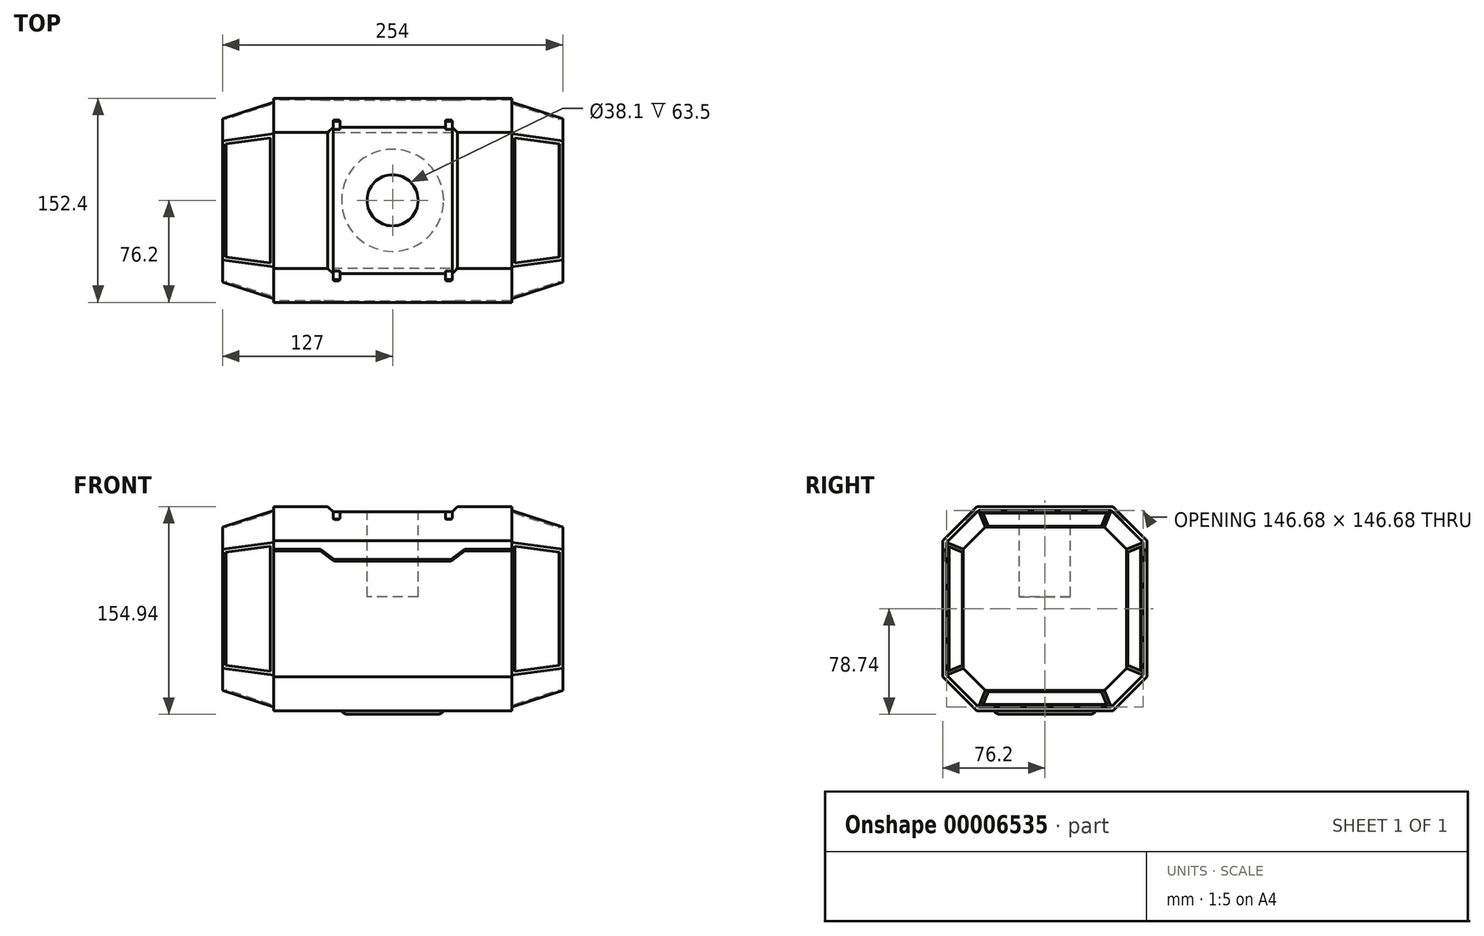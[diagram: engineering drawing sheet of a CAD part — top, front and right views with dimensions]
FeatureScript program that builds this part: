
annotation { "Feature Type Name" : "Feature", "Feature Type Description" : "" }
export const myFeature = defineFeature(function(context is Context, id is Id, definition is map)
    precondition{}
    {
        {
            var Q0;
            Q0=qCreatedBy(makeId("Top.planeOp"),FACE);
            var sketch = newSketch(context, id + "F0", { "sketchPlane" : qUnion([Q0])});
            skLineSegment(sketch, "E0.bottom", {"start": v(-88.9, -76.2) * mm, "end": v(88.9, -76.2) * mm});
            skLineSegment(sketch, "E0.top", {"start": v(-88.9, 76.2) * mm, "end": v(88.9, 76.2) * mm});
            skLineSegment(sketch, "E0.left", {"start": v(-88.9, -76.2) * mm, "end": v(-88.9, 76.2) * mm});
            skLineSegment(sketch, "E0.right", {"start": v(88.9, -76.2) * mm, "end": v(88.9, 76.2) * mm});
            skSolve(sketch);
        }
        {
            var Q0;
            Q0=makeQuery(id+"F0.imprint","IMPRINT",FACE,{"disambiguationData":[TD([[makeQuery(id+"F0.imprint","IMPRINT",EDGE,{"derivedFrom":sQuery(id+"F0.wireOp",EDGE,"E0.bottom")}),1.0]])]});
            extrude(context, id + "F1", {"entities" : qUnion([Q0]), "depth" : 152.4 * mm});
        }
        {
            var Q0;
            Q0=makeQuery(id+"F1.opExtrude","CAP_EDGE",EDGE,{"disambiguationData":[OSD([sQuery(id+"F0.wireOp",EDGE,"E0.bottom")])],"isStart":false});
            var Q1;
            Q1=makeQuery(id+"F1.opExtrude","CAP_EDGE",EDGE,{"disambiguationData":[OSD([sQuery(id+"F0.wireOp",EDGE,"E0.top")])],"isStart":false});
            var Q2;
            Q2=makeQuery(id+"F1.opExtrude","CAP_EDGE",EDGE,{"disambiguationData":[OSD([sQuery(id+"F0.wireOp",EDGE,"E0.bottom")])],"isStart":true});
            var Q3;
            Q3=makeQuery(id+"F1.opExtrude","CAP_EDGE",EDGE,{"disambiguationData":[OSD([sQuery(id+"F0.wireOp",EDGE,"E0.top")])],"isStart":true});
            chamfer(context, id + "F2", {"entities" : qUnion([Q0, Q1, Q2, Q3]), "width" : 25.4 * mm, "tangentPropagation" : true});
        }
        {
            var Q0;
            Q0=makeQuery(id+"F1.opExtrude","SWEPT_FACE",FACE,{"disambiguationData":[OSD([sQuery(id+"F0.wireOp",EDGE,"E0.left")])]});
            var sketch = newSketch(context, id + "F3", { "sketchPlane" : qUnion([Q0])});
            skLineSegment(sketch, "E1.0", {"start": v(-49.75, 149.86) * mm, "end": v(-73.66, 125.95) * mm});
            skLineSegment(sketch, "E1.1", {"start": v(49.75, 149.86) * mm, "end": v(-49.75, 149.86) * mm});
            skLineSegment(sketch, "E1.2", {"start": v(73.66, 125.95) * mm, "end": v(49.75, 149.86) * mm});
            skLineSegment(sketch, "E1.3", {"start": v(73.66, 26.45) * mm, "end": v(73.66, 125.95) * mm});
            skLineSegment(sketch, "E1.4", {"start": v(49.75, 2.54) * mm, "end": v(73.66, 26.45) * mm});
            skLineSegment(sketch, "E1.5", {"start": v(-73.66, 125.95) * mm, "end": v(-73.66, 26.45) * mm});
            skLineSegment(sketch, "E1.6", {"start": v(-49.75, 2.54) * mm, "end": v(49.75, 2.54) * mm});
            skLineSegment(sketch, "E1.7", {"start": v(-73.66, 26.45) * mm, "end": v(-49.75, 2.54) * mm});
            skSolve(sketch);
        }
        {
            var Q0;
            Q0=makeQuery(id+"F3.imprint","IMPRINT",FACE,{"disambiguationData":[TD([[makeQuery(id+"F3.imprint","IMPRINT",EDGE,{"derivedFrom":sQuery(id+"F3.wireOp",EDGE,"E1.0")}),1.0]])]});
            extrude(context, id + "F4", {"entities" : qUnion([Q0]), "operationType" : NewBodyOperationType.ADD, "depth" : 38.1 * mm});
        }
        {
            var Q0;
            Q0=makeQuery(id+"F4.opExtrude","CAP_FACE",FACE,{"disambiguationData":[OSD([sQuery(id+"F3.wireOp",EDGE,"E1.0"),sQuery(id+"F3.wireOp",EDGE,"E1.1"),sQuery(id+"F3.wireOp",EDGE,"E1.2"),sQuery(id+"F3.wireOp",EDGE,"E1.3"),sQuery(id+"F3.wireOp",EDGE,"E1.4"),sQuery(id+"F3.wireOp",EDGE,"E1.5"),sQuery(id+"F3.wireOp",EDGE,"E1.6"),sQuery(id+"F3.wireOp",EDGE,"E1.7")])],"isStart":false});
            chamfer(context, id + "F5", {"entities" : qUnion([Q0]), "chamferType" : ChamferType.OFFSET_ANGLE, "width" : 12.7 * mm, "oppositeDirection" : false, "angle" : 72 * degree, "tangentPropagation" : true});
        }
        {
            var Q0;
            Q0=makeQuery(id+"F1.opExtrude","SWEPT_FACE",FACE,{"disambiguationData":[OSD([sQuery(id+"F0.wireOp",EDGE,"E0.right")])]});
            var sketch = newSketch(context, id + "F6", { "sketchPlane" : qUnion([Q0])});
            skLineSegment(sketch, "E2.0", {"start": v(-73.66, 26.45) * mm, "end": v(-49.75, 2.54) * mm});
            skLineSegment(sketch, "E2.1", {"start": v(-73.66, 125.95) * mm, "end": v(-73.66, 26.45) * mm});
            skLineSegment(sketch, "E2.2", {"start": v(-49.75, 149.86) * mm, "end": v(-73.66, 125.95) * mm});
            skLineSegment(sketch, "E2.3", {"start": v(49.75, 149.86) * mm, "end": v(-49.75, 149.86) * mm});
            skLineSegment(sketch, "E2.4", {"start": v(73.66, 125.95) * mm, "end": v(49.75, 149.86) * mm});
            skLineSegment(sketch, "E2.5", {"start": v(-49.75, 2.54) * mm, "end": v(49.75, 2.54) * mm});
            skLineSegment(sketch, "E2.6", {"start": v(73.66, 26.45) * mm, "end": v(73.66, 125.95) * mm});
            skLineSegment(sketch, "E2.7", {"start": v(49.75, 2.54) * mm, "end": v(73.66, 26.45) * mm});
            skSolve(sketch);
        }
        {
            var Q0;
            Q0=makeQuery(id+"F6.imprint","IMPRINT",FACE,{"disambiguationData":[TD([[makeQuery(id+"F6.imprint","IMPRINT",EDGE,{"derivedFrom":sQuery(id+"F6.wireOp",EDGE,"E2.0")}),1.0]])]});
            extrude(context, id + "F7", {"entities" : qUnion([Q0]), "operationType" : NewBodyOperationType.ADD, "depth" : 38.1 * mm});
        }
        {
            var Q0;
            Q0=makeQuery(id+"F7.opExtrude","CAP_FACE",FACE,{"disambiguationData":[OSD([sQuery(id+"F6.wireOp",EDGE,"E2.0"),sQuery(id+"F6.wireOp",EDGE,"E2.1"),sQuery(id+"F6.wireOp",EDGE,"E2.2"),sQuery(id+"F6.wireOp",EDGE,"E2.3"),sQuery(id+"F6.wireOp",EDGE,"E2.4"),sQuery(id+"F6.wireOp",EDGE,"E2.5"),sQuery(id+"F6.wireOp",EDGE,"E2.6"),sQuery(id+"F6.wireOp",EDGE,"E2.7")])],"isStart":false});
            chamfer(context, id + "F8", {"entities" : qUnion([Q0]), "chamferType" : ChamferType.OFFSET_ANGLE, "width" : 12.7 * mm, "oppositeDirection" : false, "angle" : 72 * degree, "tangentPropagation" : true});
        }
        {
            var Q0;
            Q0=makeQuery(id+"F1.opExtrude","CAP_FACE",FACE,{"disambiguationData":[OSD([sQuery(id+"F0.wireOp",EDGE,"E0.bottom"),sQuery(id+"F0.wireOp",EDGE,"E0.top"),sQuery(id+"F0.wireOp",EDGE,"E0.left"),sQuery(id+"F0.wireOp",EDGE,"E0.right")])],"isStart":true});
            var sketch = newSketch(context, id + "F9", { "sketchPlane" : qUnion([Q0])});
            skCircle(sketch, "E3", {"center": v(0, 0) * mm, "radius": 38.1 * mm});
            skSolve(sketch);
        }
        {
            var Q0;
            Q0=makeQuery(id+"F9.imprint","IMPRINT",FACE,{"disambiguationData":[TD([[makeQuery(id+"F9.imprint","IMPRINT",EDGE,{"derivedFrom":sQuery(id+"F9.wireOp",EDGE,"E3")}),1.0]])]});
            extrude(context, id + "F10", {"entities" : qUnion([Q0]), "operationType" : NewBodyOperationType.ADD, "depth" : 2.54 * mm});
        }
        {
            var Q0;
            Q0=makeQuery(id+"F10.opExtrude","CAP_EDGE",EDGE,{"disambiguationData":[OSD([sQuery(id+"F9.wireOp",EDGE,"E3")])],"isStart":false});
            fillet(context, id + "F11", {"entities" : qUnion([Q0]), "radius" : 5.08 * mm, "tangentPropagation" : true, "allowEdgeOverflow" : false});
        }
        {
            var Q0;
            Q0=makeQuery(id+"F1.opExtrude","SWEPT_FACE",FACE,{"disambiguationData":[OSD([sQuery(id+"F0.wireOp",EDGE,"E0.bottom")])]});
            var sketch = newSketch(context, id + "F12", { "sketchPlane" : qUnion([Q0])});
            skLineSegment(sketch, "E4", {"start": v(0, 148.6) * mm, "end": v(44.45, 148.6) * mm});
            skLineSegment(sketch, "E5", {"start": v(44.45, 148.6) * mm, "end": v(51.87, 155.65) * mm});
            skLineSegment(sketch, "E6.0.MirrorCS", {"start": v(0, 148.6) * mm, "end": v(-44.45, 148.6) * mm});
            skLineSegment(sketch, "E7.0.MirrorCS", {"start": v(-44.45, 148.6) * mm, "end": v(-51.87, 155.65) * mm});
            skLineSegment(sketch, "E8", {"start": v(-51.87, 155.65) * mm, "end": v(51.87, 155.65) * mm});
            skSolve(sketch);
        }
        {
            var Q0;
            Q0=makeQuery(id+"F12.imprint","IMPRINT",FACE,{"disambiguationData":[TD([[makeQuery(id+"F12.imprint","IMPRINT",EDGE,{"derivedFrom":sQuery(id+"F12.wireOp",EDGE,"E4")}),1.0]])]});
            extrude(context, id + "F13", {"entities" : qUnion([Q0]), "operationType" : NewBodyOperationType.REMOVE, "oppositeDirection" : true, "depth" : 152.4 * mm});
        }
        {
            var Q0;
            {var subQ0=sQuery(id+"F0.wireOp",EDGE,"E0.top");Q0=makeQuery(id+"F2.opChamfer","BLEND_FACE",FACE,{"disambiguationData":[OSD([subQ0]),TDD([makeQuery(id+"F1.opExtrude","CAP_EDGE",EDGE,{"disambiguationData":[OSD([subQ0])],"isStart":false})])]});}
            var sketch = newSketch(context, id + "F14", { "sketchPlane" : qUnion([Q0])});
            skLineSegment(sketch, "E9.bottom", {"start": v(-44.45, 66.45) * mm, "end": v(-39.37, 66.45) * mm});
            skLineSegment(sketch, "E9.top", {"start": v(-43.18, 58.83) * mm, "end": v(-40.64, 58.83) * mm});
            skLineSegment(sketch, "E9.left", {"start": v(-44.45, 66.45) * mm, "end": v(-44.45, 60.1) * mm});
            skLineSegment(sketch, "E9.right", {"start": v(-39.37, 66.45) * mm, "end": v(-39.37, 60.1) * mm});
            skLineSegment(sketch, "E10.bottom", {"start": v(44.45, 66.45) * mm, "end": v(39.37, 66.45) * mm});
            skLineSegment(sketch, "E10.top", {"start": v(43.18, 58.83) * mm, "end": v(40.64, 58.83) * mm});
            skLineSegment(sketch, "E10.left", {"start": v(44.45, 66.45) * mm, "end": v(44.45, 60.1) * mm});
            skLineSegment(sketch, "E10.right", {"start": v(39.37, 66.45) * mm, "end": v(39.37, 60.1) * mm});
            skPoint(sketch, "E11.visualSharp", {"position": v(-44.45, 58.83) * mm});
            skArc(sketch, "E11.filletArc", {"start": v(-44.45, 60.1) * mm, "mid": v(-44.08, 59.2) * mm, "end": v(-43.18, 58.83) * mm});
            skPoint(sketch, "E12.visualSharp", {"position": v(-39.37, 58.83) * mm});
            skArc(sketch, "E12.filletArc", {"start": v(-40.64, 58.83) * mm, "mid": v(-39.74, 59.2) * mm, "end": v(-39.37, 60.1) * mm});
            skPoint(sketch, "E13.visualSharp", {"position": v(39.37, 58.83) * mm});
            skArc(sketch, "E13.filletArc", {"start": v(39.37, 60.1) * mm, "mid": v(39.74, 59.2) * mm, "end": v(40.64, 58.83) * mm});
            skPoint(sketch, "E14.visualSharp", {"position": v(44.45, 58.83) * mm});
            skArc(sketch, "E14.filletArc", {"start": v(43.18, 58.83) * mm, "mid": v(44.08, 59.2) * mm, "end": v(44.45, 60.1) * mm});
            skLineSegment(sketch, "E15.top", {"start": v(-44.45, 69.9) * mm, "end": v(-39.37, 69.9) * mm});
            skLineSegment(sketch, "E15.left", {"start": v(-44.45, 66.45) * mm, "end": v(-44.45, 69.9) * mm});
            skLineSegment(sketch, "E15.right", {"start": v(-39.37, 66.45) * mm, "end": v(-39.37, 69.9) * mm});
            skLineSegment(sketch, "E16.top", {"start": v(44.45, 69.9) * mm, "end": v(39.37, 69.9) * mm});
            skLineSegment(sketch, "E16.left", {"start": v(44.45, 66.45) * mm, "end": v(44.45, 69.9) * mm});
            skLineSegment(sketch, "E16.right", {"start": v(39.37, 66.45) * mm, "end": v(39.37, 69.9) * mm});
            skSolve(sketch);
        }
        {
            var Q0;
            Q0=makeQuery(id+"F14.imprint","IMPRINT",FACE,{"disambiguationData":[TD([[makeQuery(id+"F14.imprint","IMPRINT",EDGE,{"derivedFrom":sQuery(id+"F14.wireOp",EDGE,"E9.top")}),1.0]])]});
            var Q1;
            Q1=makeQuery(id+"F14.imprint","IMPRINT",FACE,{"disambiguationData":[TD([[makeQuery(id+"F14.imprint","IMPRINT",EDGE,{"derivedFrom":sQuery(id+"F14.wireOp",EDGE,"E9.bottom")}),-1.0]])]});
            var Q2;
            Q2=makeQuery(id+"F14.imprint","IMPRINT",FACE,{"disambiguationData":[TD([[makeQuery(id+"F14.imprint","IMPRINT",EDGE,{"derivedFrom":sQuery(id+"F14.wireOp",EDGE,"E10.top")}),-1.0]])]});
            var Q3;
            Q3=makeQuery(id+"F14.imprint","IMPRINT",FACE,{"disambiguationData":[TD([[makeQuery(id+"F14.imprint","IMPRINT",EDGE,{"derivedFrom":sQuery(id+"F14.wireOp",EDGE,"E10.bottom")}),-1.0]])]});
            extrude(context, id + "F15", {"entities" : qUnion([Q0, Q1, Q2, Q3]), "operationType" : NewBodyOperationType.REMOVE, "oppositeDirection" : true, "depth" : 1.27 * mm});
        }
        {
            var Q0;
            {var subQ0=sQuery(id+"F0.wireOp",EDGE,"E0.bottom");Q0=makeQuery(id+"F2.opChamfer","BLEND_FACE",FACE,{"disambiguationData":[OSD([subQ0]),TDD([makeQuery(id+"F1.opExtrude","CAP_EDGE",EDGE,{"disambiguationData":[OSD([subQ0])],"isStart":false})])]});}
            var sketch = newSketch(context, id + "F16", { "sketchPlane" : qUnion([Q0])});
            skLineSegment(sketch, "E17.bottom", {"start": v(-44.45, 66.45) * mm, "end": v(-39.37, 66.45) * mm});
            skLineSegment(sketch, "E17.top", {"start": v(-43.18, 58.83) * mm, "end": v(-40.64, 58.83) * mm});
            skLineSegment(sketch, "E17.left", {"start": v(-44.45, 66.45) * mm, "end": v(-44.45, 60.1) * mm});
            skLineSegment(sketch, "E17.right", {"start": v(-39.37, 66.45) * mm, "end": v(-39.37, 60.1) * mm});
            skLineSegment(sketch, "E18.bottom", {"start": v(44.45, 66.45) * mm, "end": v(39.37, 66.45) * mm});
            skLineSegment(sketch, "E18.top", {"start": v(43.18, 58.83) * mm, "end": v(40.64, 58.83) * mm});
            skLineSegment(sketch, "E18.left", {"start": v(44.45, 66.45) * mm, "end": v(44.45, 60.1) * mm});
            skLineSegment(sketch, "E18.right", {"start": v(39.37, 66.45) * mm, "end": v(39.37, 60.1) * mm});
            skPoint(sketch, "E19.visualSharp", {"position": v(-44.45, 58.83) * mm});
            skArc(sketch, "E19.filletArc", {"start": v(-44.45, 60.1) * mm, "mid": v(-44.08, 59.2) * mm, "end": v(-43.18, 58.83) * mm});
            skPoint(sketch, "E20.visualSharp", {"position": v(-39.37, 58.83) * mm});
            skArc(sketch, "E20.filletArc", {"start": v(-40.64, 58.83) * mm, "mid": v(-39.74, 59.2) * mm, "end": v(-39.37, 60.1) * mm});
            skPoint(sketch, "E21.visualSharp", {"position": v(39.37, 58.83) * mm});
            skArc(sketch, "E21.filletArc", {"start": v(39.37, 60.1) * mm, "mid": v(39.74, 59.2) * mm, "end": v(40.64, 58.83) * mm});
            skPoint(sketch, "E22.visualSharp", {"position": v(44.45, 58.83) * mm});
            skArc(sketch, "E22.filletArc", {"start": v(43.18, 58.83) * mm, "mid": v(44.08, 59.2) * mm, "end": v(44.45, 60.1) * mm});
            skLineSegment(sketch, "E23.top", {"start": v(-44.45, 70.2) * mm, "end": v(-39.37, 70.2) * mm});
            skLineSegment(sketch, "E23.left", {"start": v(-44.45, 66.45) * mm, "end": v(-44.45, 70.2) * mm});
            skLineSegment(sketch, "E23.right", {"start": v(-39.37, 66.45) * mm, "end": v(-39.37, 70.2) * mm});
            skLineSegment(sketch, "E24.top", {"start": v(44.45, 71) * mm, "end": v(39.37, 71) * mm});
            skLineSegment(sketch, "E24.left", {"start": v(44.45, 66.45) * mm, "end": v(44.45, 71) * mm});
            skLineSegment(sketch, "E24.right", {"start": v(39.37, 66.45) * mm, "end": v(39.37, 71) * mm});
            skSolve(sketch);
        }
        {
            var Q0;
            Q0=makeQuery(id+"F16.imprint","IMPRINT",FACE,{"disambiguationData":[TD([[makeQuery(id+"F16.imprint","IMPRINT",EDGE,{"derivedFrom":sQuery(id+"F16.wireOp",EDGE,"E17.top")}),1.0]])]});
            var Q1;
            Q1=makeQuery(id+"F16.imprint","IMPRINT",FACE,{"disambiguationData":[TD([[makeQuery(id+"F16.imprint","IMPRINT",EDGE,{"derivedFrom":sQuery(id+"F16.wireOp",EDGE,"E17.bottom")}),-1.0]])]});
            var Q2;
            Q2=makeQuery(id+"F16.imprint","IMPRINT",FACE,{"disambiguationData":[TD([[makeQuery(id+"F16.imprint","IMPRINT",EDGE,{"derivedFrom":sQuery(id+"F16.wireOp",EDGE,"E18.top")}),-1.0]])]});
            var Q3;
            Q3=makeQuery(id+"F16.imprint","IMPRINT",FACE,{"disambiguationData":[TD([[makeQuery(id+"F16.imprint","IMPRINT",EDGE,{"derivedFrom":sQuery(id+"F16.wireOp",EDGE,"E18.bottom")}),-1.0]])]});
            extrude(context, id + "F17", {"entities" : qUnion([Q0, Q1, Q2, Q3]), "operationType" : NewBodyOperationType.REMOVE, "oppositeDirection" : true, "depth" : 1.27 * mm});
        }
        {
            var Q0;
            Q0=makeQuery(id+"F1.opExtrude","SWEPT_FACE",FACE,{"disambiguationData":[OSD([sQuery(id+"F0.wireOp",EDGE,"E0.bottom")])]});
            var sketch = newSketch(context, id + "F18", { "sketchPlane" : qUnion([Q0])});
            skLineSegment(sketch, "E25", {"start": v(88.9, 120.65) * mm, "end": v(53.9, 120.65) * mm});
            skLineSegment(sketch, "E26", {"start": v(0, 113.03) * mm, "end": v(43.78, 113.03) * mm});
            skLineSegment(sketch, "E27", {"start": v(43.78, 113.03) * mm, "end": v(53.9, 120.65) * mm});
            skLineSegment(sketch, "E28.0.MirrorCS", {"start": v(0, 113.03) * mm, "end": v(-43.78, 113.03) * mm});
            skLineSegment(sketch, "E29.0.MirrorCS", {"start": v(-43.78, 113.03) * mm, "end": v(-53.9, 120.65) * mm});
            skLineSegment(sketch, "E30.trimOffspring", {"start": v(-53.9, 120.65) * mm, "end": v(-88.9, 120.65) * mm});
            skPoint(sketch, "E31.orphan", {"position": v(0, 120.65) * mm});
            skLineSegment(sketch, "E32.0", {"start": v(0, 111.76) * mm, "end": v(43.78, 111.76) * mm});
            skLineSegment(sketch, "E32.1", {"start": v(0, 111.76) * mm, "end": v(-43.78, 111.76) * mm});
            skLineSegment(sketch, "E33.0", {"start": v(88.9, 119.38) * mm, "end": v(53.94, 119.38) * mm});
            skLineSegment(sketch, "E34.0", {"start": v(-53.9, 119.38) * mm, "end": v(-88.9, 119.38) * mm});
            skLineSegment(sketch, "E35", {"start": v(-53.9, 119.38) * mm, "end": v(-43.78, 111.76) * mm});
            skLineSegment(sketch, "E36", {"start": v(53.94, 119.38) * mm, "end": v(43.78, 111.76) * mm});
            skSolve(sketch);
        }
        {
            var Q0;
            Q0=makeQuery(id+"F1.opExtrude","SWEPT_FACE",FACE,{"disambiguationData":[OSD([sQuery(id+"F0.wireOp",EDGE,"E0.top")])]});
            var sketch = newSketch(context, id + "F19", { "sketchPlane" : qUnion([Q0])});
            skLineSegment(sketch, "E37.0", {"start": v(0, 111.76) * mm, "end": v(43.78, 111.76) * mm});
            skLineSegment(sketch, "E38.0", {"start": v(0, 113.03) * mm, "end": v(-43.78, 113.03) * mm});
            skLineSegment(sketch, "E39.0", {"start": v(0, 111.76) * mm, "end": v(-43.78, 111.76) * mm});
            skLineSegment(sketch, "E40.0", {"start": v(-53.94, 119.38) * mm, "end": v(-43.78, 111.76) * mm});
            skLineSegment(sketch, "E40.1", {"start": v(-43.78, 113.03) * mm, "end": v(-53.9, 120.65) * mm});
            skLineSegment(sketch, "E41.0", {"start": v(-88.9, 119.38) * mm, "end": v(-53.94, 119.38) * mm});
            skLineSegment(sketch, "E41.1", {"start": v(-88.9, 120.65) * mm, "end": v(-53.9, 120.65) * mm});
            skLineSegment(sketch, "E42.0", {"start": v(53.9, 119.38) * mm, "end": v(88.9, 119.38) * mm});
            skLineSegment(sketch, "E42.1", {"start": v(53.9, 120.65) * mm, "end": v(88.9, 120.65) * mm});
            skLineSegment(sketch, "E43.0", {"start": v(53.9, 119.38) * mm, "end": v(43.78, 111.76) * mm});
            skLineSegment(sketch, "E43.1", {"start": v(43.78, 113.03) * mm, "end": v(53.9, 120.65) * mm});
            skLineSegment(sketch, "E43.2", {"start": v(0, 113.03) * mm, "end": v(43.78, 113.03) * mm});
            skSolve(sketch);
        }
        {
            var Q0;
            Q0=makeQuery(id+"F19.imprint","IMPRINT",FACE,{"disambiguationData":[TD([[makeQuery(id+"F19.imprint","IMPRINT",EDGE,{"derivedFrom":sQuery(id+"F19.wireOp",EDGE,"E37.0")}),1.0]])]});
            extrude(context, id + "F20", {"entities" : qUnion([Q0]), "operationType" : NewBodyOperationType.REMOVE, "oppositeDirection" : true, "depth" : 1.27 * mm});
        }
        {
            var Q0;
            {var subQ6=sQuery(id+"F18.wireOp",EDGE,"E25");Q0=makeQuery(id+"F18.imprint","IMPRINT",FACE,{"disambiguationData":[TD([[makeQuery(id+"F18.imprint","IMPRINT",EDGE,{"derivedFrom":subQ6}),1.0]])]});}
            extrude(context, id + "F21", {"entities" : qUnion([Q0]), "operationType" : NewBodyOperationType.REMOVE, "oppositeDirection" : true, "depth" : 1.27 * mm});
        }
        {
            var Q0;
            Q0=makeQuery(id+"F13.boolean.opBoolean","COPY",FACE,{"derivedFrom":makeQuery(id+"F13.opExtrude","SWEPT_FACE",FACE,{"disambiguationData":[OSD([sQuery(id+"F12.wireOp",EDGE,"E4"),sQuery(id+"F12.wireOp",EDGE,"E6.0.MirrorCS")])]})});
            var sketch = newSketch(context, id + "F22", { "sketchPlane" : qUnion([Q0])});
            skCircle(sketch, "E44", {"center": v(0, 0) * mm, "radius": 19.05 * mm});
            skSolve(sketch);
        }
        {
            var Q0;
            Q0=makeQuery(id+"F22.imprint","IMPRINT",FACE,{"disambiguationData":[TD([[makeQuery(id+"F22.imprint","IMPRINT",EDGE,{"derivedFrom":sQuery(id+"F22.wireOp",EDGE,"E44")}),1.0]])]});
            extrude(context, id + "F23", {"entities" : qUnion([Q0]), "operationType" : NewBodyOperationType.REMOVE, "oppositeDirection" : true, "depth" : 63.5 * mm});
        }
        {
            var Q0;
            Q0=makeQuery(id+"F8.opChamfer","BLEND_FACE",FACE,{"disambiguationData":[OSD([sQuery(id+"F6.wireOp",EDGE,"E2.3")])]});
            var sketch = newSketch(context, id + "F24", { "sketchPlane" : qUnion([Q0])});
            skLineSegment(sketch, "E45.0", {"start": v(40.88, -46.73) * mm, "end": v(75.86, -42.25) * mm});
            skLineSegment(sketch, "E45.1", {"start": v(40.88, 46.73) * mm, "end": v(40.88, -46.73) * mm});
            skLineSegment(sketch, "E45.2", {"start": v(40.88, 46.73) * mm, "end": v(75.86, 42.25) * mm});
            skLineSegment(sketch, "E45.3", {"start": v(75.86, -42.25) * mm, "end": v(75.86, 42.25) * mm});
            skSolve(sketch);
        }
        {
            var Q0;
            Q0=makeQuery(id+"F24.imprint","IMPRINT",FACE,{"disambiguationData":[TD([[makeQuery(id+"F24.imprint","IMPRINT",EDGE,{"derivedFrom":sQuery(id+"F24.wireOp",EDGE,"E45.0")}),1.0]])]});
            extrude(context, id + "F25", {"entities" : qUnion([Q0]), "operationType" : NewBodyOperationType.REMOVE, "oppositeDirection" : true, "depth" : 1.27 * mm});
        }
        {
            var Q0;
            Q0=qCreatedBy(makeId("Front.planeOp"),FACE);
            var sketch = newSketch(context, id + "F26", { "sketchPlane" : qUnion([Q0])});
            skLineSegment(sketch, "E46", {"start": v(0, 76.2) * mm, "end": v(-188.8, 76.2) * mm});
            skSolve(sketch);
        }
        {
            var Q0;
            Q0=makeQuery(id+"F25.boolean.opBoolean","COPY",FACE,{"derivedFrom":makeQuery(id+"F25.opExtrude","CAP_FACE",FACE,{"disambiguationData":[OSD([sQuery(id+"F24.wireOp",EDGE,"E45.0"),sQuery(id+"F24.wireOp",EDGE,"E45.1"),sQuery(id+"F24.wireOp",EDGE,"E45.2"),sQuery(id+"F24.wireOp",EDGE,"E45.3")])],"isStart":false})});
            var Q1;
            Q1=makeQuery(id+"F25.boolean.opBoolean","COPY",FACE,{"derivedFrom":makeQuery(id+"F25.opExtrude","SWEPT_FACE",FACE,{"disambiguationData":[OSD([sQuery(id+"F24.wireOp",EDGE,"E45.3")])]})});
            var Q2;
            Q2=makeQuery(id+"F25.boolean.opBoolean","COPY",FACE,{"derivedFrom":makeQuery(id+"F25.opExtrude","SWEPT_FACE",FACE,{"disambiguationData":[OSD([sQuery(id+"F24.wireOp",EDGE,"E45.0")])]})});
            var Q3;
            Q3=makeQuery(id+"F25.boolean.opBoolean","COPY",FACE,{"derivedFrom":makeQuery(id+"F25.opExtrude","SWEPT_FACE",FACE,{"disambiguationData":[OSD([sQuery(id+"F24.wireOp",EDGE,"E45.1")])]})});
            var Q4;
            Q4=makeQuery(id+"F25.boolean.opBoolean","COPY",FACE,{"derivedFrom":makeQuery(id+"F25.opExtrude","SWEPT_FACE",FACE,{"disambiguationData":[OSD([sQuery(id+"F24.wireOp",EDGE,"E45.2")])]})});
            var Q5;
            Q5=sQuery(id+"F26.wireOp",EDGE,"E46");
            circularPattern(context, id + "F27", {"faces" : qUnion([Q0, Q1, Q2, Q3, Q4]), "axis" : qUnion([Q5]), "angle" : 90 * degree, "instanceCount" : 4, "patternType" : PatternType.FACE});
        }
        {
            var Q0;
            Q0=makeQuery(id+"F5.opChamfer","BLEND_FACE",FACE,{"disambiguationData":[OSD([sQuery(id+"F3.wireOp",EDGE,"E1.6")])]});
            var sketch = newSketch(context, id + "F28", { "sketchPlane" : qUnion([Q0])});
            skLineSegment(sketch, "E47.0", {"start": v(-87.97, 46.73) * mm, "end": v(-122.95, 42.25) * mm});
            skLineSegment(sketch, "E47.1", {"start": v(-87.97, -46.73) * mm, "end": v(-87.97, 46.73) * mm});
            skLineSegment(sketch, "E47.2", {"start": v(-87.97, -46.73) * mm, "end": v(-122.95, -42.25) * mm});
            skLineSegment(sketch, "E47.3", {"start": v(-122.95, 42.25) * mm, "end": v(-122.95, -42.25) * mm});
            skSolve(sketch);
        }
        {
            var Q0;
            Q0=makeQuery(id+"F28.imprint","IMPRINT",FACE,{"disambiguationData":[TD([[makeQuery(id+"F28.imprint","IMPRINT",EDGE,{"derivedFrom":sQuery(id+"F28.wireOp",EDGE,"E47.0")}),1.0]])]});
            extrude(context, id + "F29", {"entities" : qUnion([Q0]), "operationType" : NewBodyOperationType.REMOVE, "oppositeDirection" : true, "depth" : 1.27 * mm});
        }
        {
            var Q0;
            Q0=qCreatedBy(makeId("Front.planeOp"),FACE);
            var sketch = newSketch(context, id + "F30", { "sketchPlane" : qUnion([Q0])});
            skLineSegment(sketch, "E48", {"start": v(0, 76.2) * mm, "end": v(-234.44, 76.2) * mm});
            skSolve(sketch);
        }
        {
            var Q0;
            Q0=makeQuery(id+"F29.boolean.opBoolean","COPY",FACE,{"derivedFrom":makeQuery(id+"F29.opExtrude","CAP_FACE",FACE,{"disambiguationData":[OSD([sQuery(id+"F28.wireOp",EDGE,"E47.0"),sQuery(id+"F28.wireOp",EDGE,"E47.1"),sQuery(id+"F28.wireOp",EDGE,"E47.2"),sQuery(id+"F28.wireOp",EDGE,"E47.3")])],"isStart":false})});
            var Q1;
            Q1=makeQuery(id+"F29.boolean.opBoolean","COPY",FACE,{"derivedFrom":makeQuery(id+"F29.opExtrude","SWEPT_FACE",FACE,{"disambiguationData":[OSD([sQuery(id+"F28.wireOp",EDGE,"E47.2")])]})});
            var Q2;
            Q2=makeQuery(id+"F29.boolean.opBoolean","COPY",FACE,{"derivedFrom":makeQuery(id+"F29.opExtrude","SWEPT_FACE",FACE,{"disambiguationData":[OSD([sQuery(id+"F28.wireOp",EDGE,"E47.3")])]})});
            var Q3;
            Q3=makeQuery(id+"F29.boolean.opBoolean","COPY",FACE,{"derivedFrom":makeQuery(id+"F29.opExtrude","SWEPT_FACE",FACE,{"disambiguationData":[OSD([sQuery(id+"F28.wireOp",EDGE,"E47.0")])]})});
            var Q4;
            Q4=makeQuery(id+"F29.boolean.opBoolean","COPY",FACE,{"derivedFrom":makeQuery(id+"F29.opExtrude","SWEPT_FACE",FACE,{"disambiguationData":[OSD([sQuery(id+"F28.wireOp",EDGE,"E47.1")])]})});
            var Q5;
            Q5=sQuery(id+"F30.wireOp",EDGE,"E48");
            circularPattern(context, id + "F31", {"faces" : qUnion([Q0, Q1, Q2, Q3, Q4]), "axis" : qUnion([Q5]), "angle" : 90 * degree, "instanceCount" : 4, "patternType" : PatternType.FACE});
        }
    });
